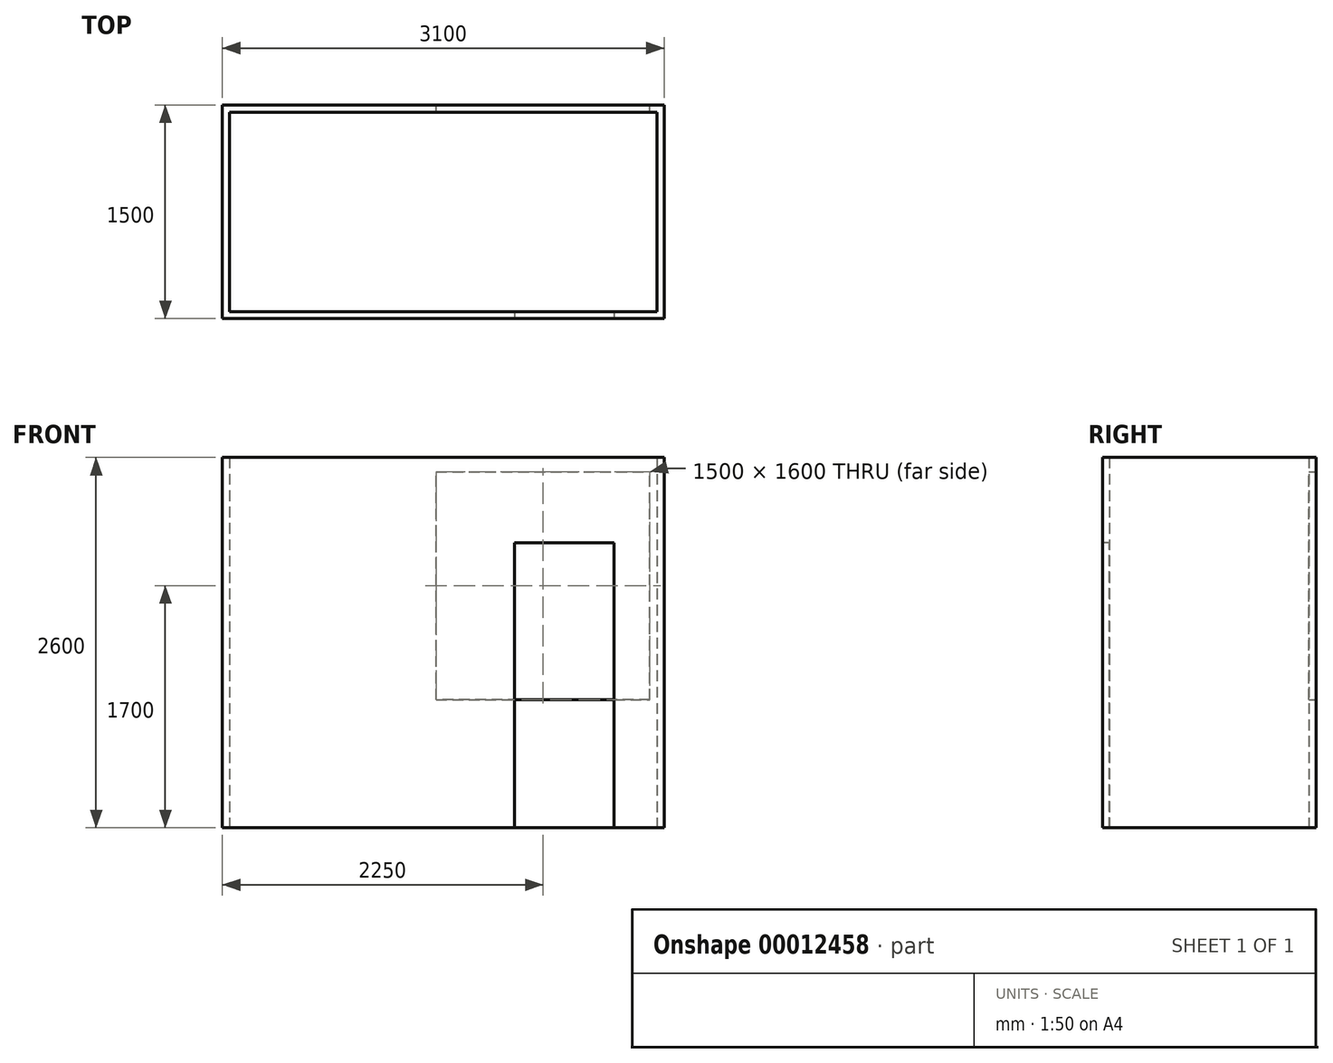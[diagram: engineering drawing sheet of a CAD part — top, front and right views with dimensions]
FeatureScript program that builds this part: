
annotation { "Feature Type Name" : "Feature", "Feature Type Description" : "" }
export const myFeature = defineFeature(function(context is Context, id is Id, definition is map)
    precondition{}
    {
        {
            var Q0;
            Q0=qCreatedBy(makeId("Top.planeOp"),FACE);
            var sketch = newSketch(context, id + "F0", { "sketchPlane" : qUnion([Q0])});
            skLineSegment(sketch, "E0.bottom", {"start": v(0, 0) * mm, "end": v(3100, 0) * mm});
            skLineSegment(sketch, "E0.top", {"start": v(0, 1500) * mm, "end": v(3100, 1500) * mm});
            skLineSegment(sketch, "E0.left", {"start": v(0, 0) * mm, "end": v(0, 1500) * mm});
            skLineSegment(sketch, "E0.right", {"start": v(3100, 0) * mm, "end": v(3100, 1500) * mm});
            skLineSegment(sketch, "E1.0", {"start": v(50, 50) * mm, "end": v(50, 1450) * mm});
            skLineSegment(sketch, "E1.1", {"start": v(50, 50) * mm, "end": v(3050, 50) * mm});
            skLineSegment(sketch, "E1.2", {"start": v(3050, 50) * mm, "end": v(3050, 1450) * mm});
            skLineSegment(sketch, "E1.3", {"start": v(50, 1450) * mm, "end": v(3050, 1450) * mm});
            skSolve(sketch);
        }
        {
            var Q0;
            Q0=makeQuery(id+"F0.imprint","IMPRINT",FACE,{"disambiguationData":[TD([[makeQuery(id+"F0.imprint","IMPRINT",EDGE,{"derivedFrom":sQuery(id+"F0.wireOp",EDGE,"E0.bottom")}),1.0]])]});
            extrude(context, id + "F1", {"entities" : qUnion([Q0]), "depth" : 2600 * mm});
        }
        {
            var Q0;
            Q0=makeQuery(id+"F1.opExtrude","SWEPT_FACE",FACE,{"disambiguationData":[OSD([sQuery(id+"F0.wireOp",EDGE,"E0.bottom")])]});
            var sketch = newSketch(context, id + "F2", { "sketchPlane" : qUnion([Q0])});
            skLineSegment(sketch, "E2", {"start": v(2050, 0) * mm, "end": v(2050, 2000) * mm});
            skLineSegment(sketch, "E3", {"start": v(2050, 2000) * mm, "end": v(2750, 2000) * mm});
            skLineSegment(sketch, "E4", {"start": v(2750, 2000) * mm, "end": v(2750, 0) * mm});
            skSolve(sketch);
        }
        {
            var Q0;
            {var subQ2=sQuery(id+"F2.wireOp",EDGE,"E2");Q0=makeQuery(id+"F2.imprint","IMPRINT",FACE,{"disambiguationData":[TD([[makeQuery(id+"F2.imprint","IMPRINT",EDGE,{"derivedFrom":subQ2}),-1.0]])]});}
            extrude(context, id + "F3", {"entities" : qUnion([Q0]), "operationType" : NewBodyOperationType.REMOVE, "endBound" : BoundingType.UP_TO_NEXT, "oppositeDirection" : true, "depth" : 25 * mm});
        }
        {
            var Q0;
            Q0=makeQuery(id+"F1.opExtrude","SWEPT_FACE",FACE,{"disambiguationData":[OSD([sQuery(id+"F0.wireOp",EDGE,"E0.top")])]});
            var sketch = newSketch(context, id + "F4", { "sketchPlane" : qUnion([Q0])});
            skLineSegment(sketch, "E5.bottom", {"start": v(-3000, 2500) * mm, "end": v(-1500, 2500) * mm});
            skLineSegment(sketch, "E5.top", {"start": v(-3000, 900) * mm, "end": v(-1500, 900) * mm});
            skLineSegment(sketch, "E5.left", {"start": v(-3000, 2500) * mm, "end": v(-3000, 900) * mm});
            skLineSegment(sketch, "E5.right", {"start": v(-1500, 2500) * mm, "end": v(-1500, 900) * mm});
            skSolve(sketch);
        }
        {
            var Q0;
            Q0=makeQuery(id+"F4.imprint","IMPRINT",FACE,{"disambiguationData":[TD([[makeQuery(id+"F4.imprint","IMPRINT",EDGE,{"derivedFrom":sQuery(id+"F4.wireOp",EDGE,"E5.bottom")}),-1.0]])]});
            extrude(context, id + "F5", {"entities" : qUnion([Q0]), "operationType" : NewBodyOperationType.REMOVE, "endBound" : BoundingType.UP_TO_NEXT, "oppositeDirection" : true, "depth" : 25 * mm});
        }
    });
